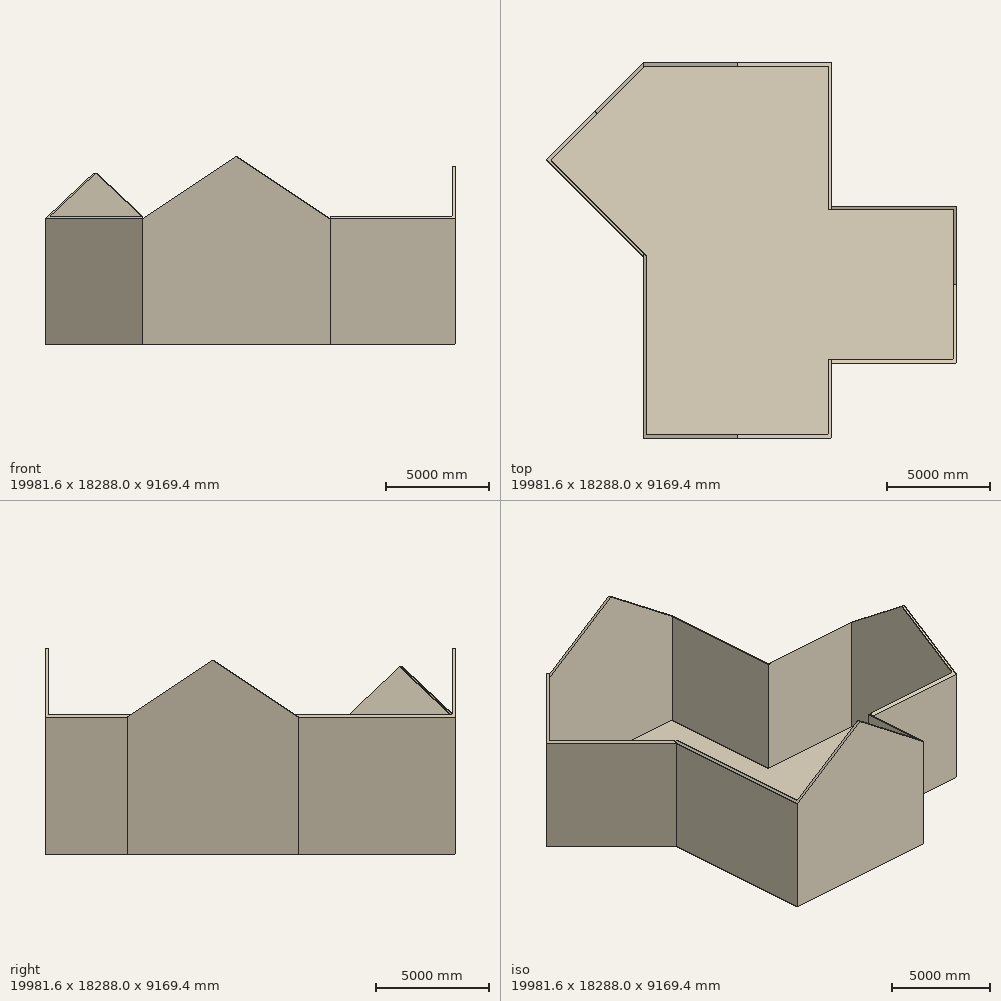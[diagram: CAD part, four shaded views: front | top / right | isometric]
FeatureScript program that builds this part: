
annotation { "Feature Type Name" : "Feature", "Feature Type Description" : "" }
export const myFeature = defineFeature(function(context is Context, id is Id, definition is map)
    precondition{}
    {
        {
            var Q0;
            Q0=qCreatedBy(makeId("Top.planeOp"),FACE);
            var sketch = newSketch(context, id + "F0", { "sketchPlane" : qUnion([Q0])});
            skLineSegment(sketch, "E0", {"start": v(0, 0) * mm, "end": v(9144, 0) * mm});
            skLineSegment(sketch, "E1", {"start": v(9144, 0) * mm, "end": v(9144, 3657.6) * mm});
            skLineSegment(sketch, "E2", {"start": v(9144, 3657.6) * mm, "end": v(15240, 3657.6) * mm});
            skLineSegment(sketch, "E3", {"start": v(15240, 3657.6) * mm, "end": v(15240, 11277.6) * mm});
            skLineSegment(sketch, "E4", {"start": v(15240, 11277.6) * mm, "end": v(9144, 11277.6) * mm});
            skLineSegment(sketch, "E5", {"start": v(9144, 11277.6) * mm, "end": v(9144, 18288) * mm});
            skLineSegment(sketch, "E6", {"start": v(9144, 18288) * mm, "end": v(0, 18288) * mm});
            skLineSegment(sketch, "E7", {"start": v(0, 18288) * mm, "end": v(-4741.58, 13546.42) * mm});
            skLineSegment(sketch, "E8", {"start": v(-4741.58, 13546.42) * mm, "end": v(0, 8804.85) * mm});
            skLineSegment(sketch, "E9", {"start": v(0, 8804.85) * mm, "end": v(0, 0) * mm});
            skSolve(sketch);
        }
        {
            var Q0;
            Q0 = qSketchRegion(id + "F0", true);
            extrude(context, id + "F1", {"entities" : qUnion([Q0]), "depth" : 25.4 * mm, "offsetDistance" : 25.4 * mm});
        }
        {
            var Q0;
            Q0=makeQuery(id+"F1.opExtrude","CAP_FACE",FACE,{"disambiguationData":[OSD([sQuery(id+"F0.wireOp",EDGE,"E0"),sQuery(id+"F0.wireOp",EDGE,"E1"),sQuery(id+"F0.wireOp",EDGE,"E2"),sQuery(id+"F0.wireOp",EDGE,"E3"),sQuery(id+"F0.wireOp",EDGE,"E4"),sQuery(id+"F0.wireOp",EDGE,"E5"),sQuery(id+"F0.wireOp",EDGE,"E6"),sQuery(id+"F0.wireOp",EDGE,"E7"),sQuery(id+"F0.wireOp",EDGE,"E8"),sQuery(id+"F0.wireOp",EDGE,"E9")])],"isStart":false});
            var sketch = newSketch(context, id + "F2", { "sketchPlane" : qUnion([Q0])});
            skLineSegment(sketch, "E10.0", {"start": v(63.13, 18135.6) * mm, "end": v(-4526.05, 13546.42) * mm});
            skLineSegment(sketch, "E10.1", {"start": v(8991.6, 18135.6) * mm, "end": v(63.13, 18135.6) * mm});
            skLineSegment(sketch, "E10.2", {"start": v(-4526.05, 13546.42) * mm, "end": v(152.4, 8867.98) * mm});
            skLineSegment(sketch, "E10.3", {"start": v(8991.6, 11125.2) * mm, "end": v(8991.6, 18135.6) * mm});
            skLineSegment(sketch, "E10.4", {"start": v(15087.6, 11125.2) * mm, "end": v(8991.6, 11125.2) * mm});
            skLineSegment(sketch, "E10.5", {"start": v(15087.6, 3810) * mm, "end": v(15087.6, 11125.2) * mm});
            skLineSegment(sketch, "E10.6", {"start": v(152.4, 8867.98) * mm, "end": v(152.4, 152.4) * mm});
            skLineSegment(sketch, "E10.7", {"start": v(152.4, 152.4) * mm, "end": v(8991.6, 152.4) * mm});
            skLineSegment(sketch, "E10.8", {"start": v(8991.6, 152.4) * mm, "end": v(8991.6, 3810) * mm});
            skLineSegment(sketch, "E10.9", {"start": v(8991.6, 3810) * mm, "end": v(15087.6, 3810) * mm});
            skLineSegment(sketch, "E11.0.0", {"start": v(-4741.58, 13546.42) * mm, "end": v(0, 8804.85) * mm});
            skLineSegment(sketch, "E11.0.1", {"start": v(0, 8804.85) * mm, "end": v(0, 0) * mm});
            skLineSegment(sketch, "E11.0.2", {"start": v(0, 0) * mm, "end": v(9144, 0) * mm});
            skLineSegment(sketch, "E11.0.3", {"start": v(9144, 0) * mm, "end": v(9144, 3657.6) * mm});
            skLineSegment(sketch, "E11.0.4", {"start": v(9144, 3657.6) * mm, "end": v(15240, 3657.6) * mm});
            skLineSegment(sketch, "E11.0.5", {"start": v(15240, 3657.6) * mm, "end": v(15240, 11277.6) * mm});
            skLineSegment(sketch, "E11.0.6", {"start": v(15240, 11277.6) * mm, "end": v(9144, 11277.6) * mm});
            skLineSegment(sketch, "E11.0.7", {"start": v(9144, 11277.6) * mm, "end": v(9144, 18288) * mm});
            skLineSegment(sketch, "E11.0.8", {"start": v(9144, 18288) * mm, "end": v(0, 18288) * mm});
            skLineSegment(sketch, "E11.0.9", {"start": v(0, 18288) * mm, "end": v(-4741.58, 13546.42) * mm});
            skSolve(sketch);
        }
        {
            var Q0;
            Q0 = qSketchRegion(id + "F2", true);
            extrude(context, id + "F3", {"entities" : qUnion([Q0]), "operationType" : NewBodyOperationType.ADD, "depth" : 9144 * mm, "offsetDistance" : 25.4 * mm});
        }
        {
            var Q0;
            Q0=makeQuery(id+"F3.boolean.opBoolean","MERGE",FACE,{"derivedFrom":[makeQuery(id+"F1.opExtrude","SWEPT_FACE",FACE,{"disambiguationData":[OSD([sQuery(id+"F0.wireOp",EDGE,"E0")])]}),makeQuery(id+"F3.opExtrude","SWEPT_FACE",FACE,{"disambiguationData":[OSD([sQuery(id+"F2.wireOp",EDGE,"E11.0.2")])]})]});
            var sketch = newSketch(context, id + "F4", { "sketchPlane" : qUnion([Q0])});
            skLineSegment(sketch, "E12", {"start": v(0, 6121.4) * mm, "end": v(4572, 9169.4) * mm});
            skLineSegment(sketch, "E13", {"start": v(4572, 9169.4) * mm, "end": v(9144, 6121.4) * mm});
            skLineSegment(sketch, "E14", {"start": v(9144, 6121.4) * mm, "end": v(9144, 9169.4) * mm});
            skLineSegment(sketch, "E15", {"start": v(9144, 9169.4) * mm, "end": v(0, 9169.4) * mm});
            skLineSegment(sketch, "E16", {"start": v(0, 9169.4) * mm, "end": v(0, 6121.4) * mm});
            skLineSegment(sketch, "E17", {"start": v(0, 6121.4) * mm, "end": v(304.8, 6121.4) * mm, "construction": true});
            skLineSegment(sketch, "E18", {"start": v(304.8, 6121.4) * mm, "end": v(304.8, 6324.6) * mm, "construction": true});
            skSolve(sketch);
        }
        {
            var Q0;
            Q0 = qSketchRegion(id + "F4", true);
            extrude(context, id + "F5", {"entities" : qUnion([Q0]), "operationType" : NewBodyOperationType.REMOVE, "endBound" : BoundingType.THROUGH_ALL, "oppositeDirection" : true, "depth" : 25.4 * mm, "offsetDistance" : 25.4 * mm});
        }
        {
            var Q0;
            Q0=makeQuery(id+"F3.boolean.opBoolean","MERGE",FACE,{"derivedFrom":[makeQuery(id+"F1.opExtrude","SWEPT_FACE",FACE,{"disambiguationData":[OSD([sQuery(id+"F0.wireOp",EDGE,"E3")])]}),makeQuery(id+"F3.opExtrude","SWEPT_FACE",FACE,{"disambiguationData":[OSD([sQuery(id+"F2.wireOp",EDGE,"E11.0.5")])]})]});
            var sketch = newSketch(context, id + "F6", { "sketchPlane" : qUnion([Q0])});
            skLineSegment(sketch, "E19", {"start": v(3657.6, 6121.4) * mm, "end": v(7467.6, 8661.4) * mm});
            skLineSegment(sketch, "E20", {"start": v(7467.6, 8661.4) * mm, "end": v(11277.6, 6121.4) * mm});
            skLineSegment(sketch, "E21", {"start": v(11277.6, 6121.4) * mm, "end": v(11277.6, 9169.4) * mm});
            skLineSegment(sketch, "E22", {"start": v(11277.6, 9169.4) * mm, "end": v(3657.6, 9169.4) * mm});
            skLineSegment(sketch, "E23", {"start": v(3657.6, 9169.4) * mm, "end": v(3657.6, 6121.4) * mm});
            skLineSegment(sketch, "E24", {"start": v(3657.6, 6121.4) * mm, "end": v(3962.4, 6121.4) * mm, "construction": true});
            skLineSegment(sketch, "E25", {"start": v(3962.4, 6121.4) * mm, "end": v(3962.4, 6324.6) * mm, "construction": true});
            skSolve(sketch);
        }
        {
            var Q0;
            Q0 = qSketchRegion(id + "F6", true);
            var Q1;
            Q1=makeQuery(id+"F5.boolean.opBoolean","COPY",FACE,{"disambiguationData":[TD([makeQuery(id+"F1.opExtrude","SWEPT_FACE",FACE,{"disambiguationData":[OSD([sQuery(id+"F0.wireOp",EDGE,"E0")])]})])],"derivedFrom":makeQuery(id+"F5.opExtrude","SWEPT_FACE",FACE,{"disambiguationData":[OSD([sQuery(id+"F4.wireOp",EDGE,"E13")])]})});
            extrude(context, id + "F7", {"entities" : qUnion([Q0]), "operationType" : NewBodyOperationType.REMOVE, "endBound" : BoundingType.UP_TO_SURFACE, "oppositeDirection" : true, "depth" : 25.4 * mm, "endBoundEntityFace" : qUnion([Q1]), "offsetDistance" : 25.4 * mm});
        }
        {
            var Q0;
            Q0=makeQuery(id+"F3.boolean.opBoolean","MERGE",FACE,{"derivedFrom":[makeQuery(id+"F1.opExtrude","SWEPT_FACE",FACE,{"disambiguationData":[OSD([sQuery(id+"F0.wireOp",EDGE,"E7")])]}),makeQuery(id+"F3.opExtrude","SWEPT_FACE",FACE,{"disambiguationData":[OSD([sQuery(id+"F2.wireOp",EDGE,"E11.0.9")])]})]});
            var sketch = newSketch(context, id + "F8", { "sketchPlane" : qUnion([Q0])});
            skLineSegment(sketch, "E26", {"start": v(-12931.57, 6121.4) * mm, "end": v(-9578.77, 8356.6) * mm});
            skLineSegment(sketch, "E27", {"start": v(-9578.77, 8356.6) * mm, "end": v(-6225.97, 6121.4) * mm});
            skLineSegment(sketch, "E28", {"start": v(-6225.97, 6121.4) * mm, "end": v(-6225.97, 9169.4) * mm});
            skLineSegment(sketch, "E29", {"start": v(-6225.97, 9169.4) * mm, "end": v(-12931.57, 9169.4) * mm});
            skLineSegment(sketch, "E30", {"start": v(-12931.57, 9169.4) * mm, "end": v(-12931.57, 6121.4) * mm});
            skLineSegment(sketch, "E31", {"start": v(-12931.57, 6121.4) * mm, "end": v(-12626.77, 6121.4) * mm, "construction": true});
            skLineSegment(sketch, "E32", {"start": v(-12626.77, 6121.4) * mm, "end": v(-12626.77, 6324.6) * mm, "construction": true});
            skSolve(sketch);
        }
        {
            var Q0;
            Q0 = qSketchRegion(id + "F8", true);
            extrude(context, id + "F9", {"entities" : qUnion([Q0]), "operationType" : NewBodyOperationType.REMOVE, "endBound" : BoundingType.UP_TO_NEXT, "oppositeDirection" : true, "depth" : 25.4 * mm, "offsetDistance" : 25.4 * mm});
        }
    });
